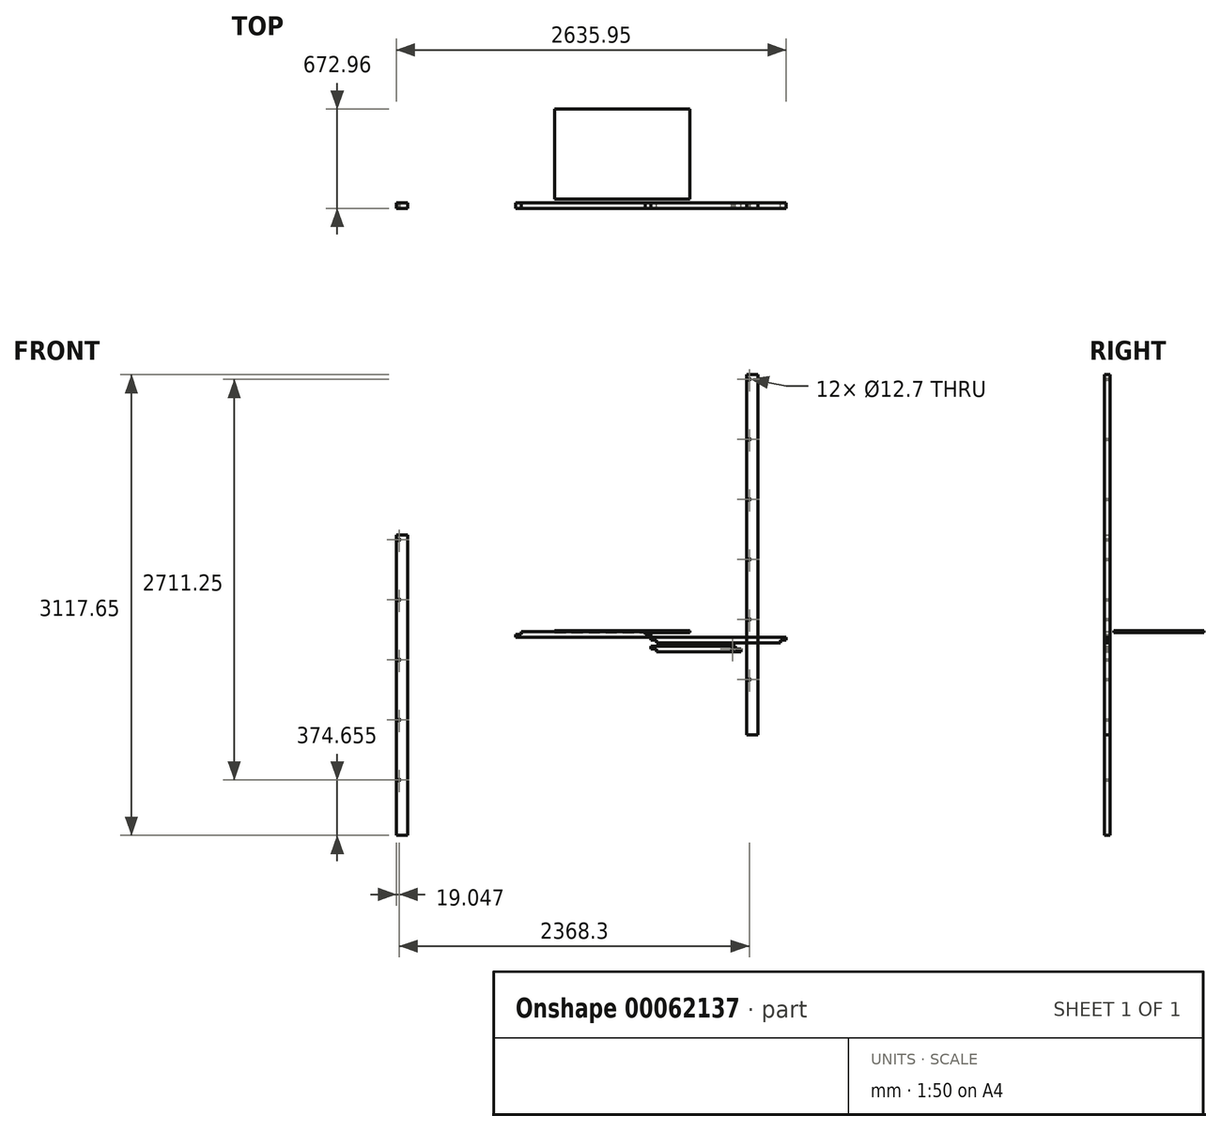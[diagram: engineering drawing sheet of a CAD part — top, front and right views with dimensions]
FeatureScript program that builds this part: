
annotation { "Feature Type Name" : "Feature", "Feature Type Description" : "" }
export const myFeature = defineFeature(function(context is Context, id is Id, definition is map)
    precondition{}
    {
        {
            var Q0;
            Q0=qCreatedBy(makeId("Top.planeOp"),FACE);
            var sketch = newSketch(context, id + "F0", { "sketchPlane" : qUnion([Q0])});
            skLineSegment(sketch, "E0.bottom", {"start": v(-1354.97, 634.86) * mm, "end": v(-440.57, 634.86) * mm});
            skLineSegment(sketch, "E0.top", {"start": v(-1354.97, 25.26) * mm, "end": v(-440.57, 25.26) * mm});
            skLineSegment(sketch, "E0.left", {"start": v(-1354.97, 634.86) * mm, "end": v(-1354.97, 25.26) * mm});
            skLineSegment(sketch, "E0.right", {"start": v(-440.57, 634.86) * mm, "end": v(-440.57, 25.26) * mm});
            skSolve(sketch);
        }
        {
            var Q0;
            Q0=qCreatedBy(makeId("Front.planeOp"),FACE);
            var sketch = newSketch(context, id + "F1", { "sketchPlane" : qUnion([Q0])});
            skLineSegment(sketch, "E1.bottom", {"start": v(-704.43, -92.97) * mm, "end": v(-132.93, -92.97) * mm});
            skLineSegment(sketch, "E1.top", {"start": v(-666.33, -131.07) * mm, "end": v(-94.83, -131.07) * mm});
            skLineSegment(sketch, "E1.left", {"start": v(-704.43, -92.97) * mm, "end": v(-704.43, -112.02) * mm});
            skLineSegment(sketch, "E1.right", {"start": v(-94.83, -112.02) * mm, "end": v(-94.83, -131.07) * mm});
            skLineSegment(sketch, "E2.top", {"start": v(-94.83, -112.02) * mm, "end": v(-132.93, -112.02) * mm});
            skLineSegment(sketch, "E2.right", {"start": v(-132.93, -92.97) * mm, "end": v(-132.93, -112.02) * mm});
            skLineSegment(sketch, "E3.top", {"start": v(-704.43, -112.02) * mm, "end": v(-666.33, -112.02) * mm});
            skLineSegment(sketch, "E3.right", {"start": v(-666.33, -131.07) * mm, "end": v(-666.33, -112.02) * mm});
            skCircle(sketch, "E4", {"center": v(-151.98, -112.02) * mm, "radius": 6.35 * mm});
            skSolve(sketch);
        }
        {
            var Q0;
            Q0=makeQuery(id+"F1.imprint","IMPRINT",FACE,{"disambiguationData":[TD([[makeQuery(id+"F1.imprint","IMPRINT",EDGE,{"derivedFrom":sQuery(id+"F1.wireOp",EDGE,"E1.bottom")}),-1.0]])]});
            extrude(context, id + "F2", {"entities" : qUnion([Q0]), "depth" : 38.1 * mm});
        }
        {
            var Q0;
            Q0=qCreatedBy(makeId("Front.planeOp"),FACE);
            var sketch = newSketch(context, id + "F3", { "sketchPlane" : qUnion([Q0])});
            skLineSegment(sketch, "E5.bottom", {"start": v(-703.85, -31.36) * mm, "end": v(210.55, -31.36) * mm});
            skLineSegment(sketch, "E5.top", {"start": v(-665.75, -69.46) * mm, "end": v(172.45, -69.46) * mm});
            skLineSegment(sketch, "E5.left", {"start": v(-703.85, -31.36) * mm, "end": v(-703.85, -50.4) * mm});
            skLineSegment(sketch, "E5.right", {"start": v(210.55, -31.36) * mm, "end": v(210.55, -50.4) * mm});
            skLineSegment(sketch, "E6.top", {"start": v(210.55, -50.4) * mm, "end": v(172.45, -50.4) * mm});
            skLineSegment(sketch, "E6.right", {"start": v(172.45, -69.46) * mm, "end": v(172.45, -50.4) * mm});
            skLineSegment(sketch, "E7.top", {"start": v(-703.85, -50.4) * mm, "end": v(-665.75, -50.4) * mm});
            skLineSegment(sketch, "E7.right", {"start": v(-665.75, -69.46) * mm, "end": v(-665.75, -50.4) * mm});
            skSolve(sketch);
        }
        {
            var Q0;
            Q0=makeQuery(id+"F3.imprint","IMPRINT",FACE,{"disambiguationData":[TD([[makeQuery(id+"F3.imprint","IMPRINT",EDGE,{"derivedFrom":sQuery(id+"F3.wireOp",EDGE,"E5.bottom")}),-1.0]])]});
            extrude(context, id + "F4", {"entities" : qUnion([Q0]), "depth" : 38.1 * mm});
        }
        {
            var Q0;
            Q0=makeQuery(id+"F4.opExtrude","SWEPT_BODY",BODY,{"disambiguationData":[OSD([sQuery(id+"F3.wireOp",EDGE,"E5.bottom"),sQuery(id+"F3.wireOp",EDGE,"E5.top"),sQuery(id+"F3.wireOp",EDGE,"E5.left"),sQuery(id+"F3.wireOp",EDGE,"E5.right"),sQuery(id+"F3.wireOp",EDGE,"E6.top"),sQuery(id+"F3.wireOp",EDGE,"E6.right"),sQuery(id+"F3.wireOp",EDGE,"E7.top"),sQuery(id+"F3.wireOp",EDGE,"E7.right")])]});
            var Q1;
            Q1=makeQuery(id+"F4.opExtrude","SWEPT_EDGE",EDGE,{"disambiguationData":[OSD([sQuery(id+"F3.wireOp",EDGE,"E5.bottom"),sQuery(id+"F3.wireOp",EDGE,"E5.left")])]});
            transform(context, id + "F5", {"entities" : qUnion([Q0]), "transformType" : TransformType.ROTATION, "transformAxis" : qUnion([Q1]), "angle" : 180 * degree, "makeCopy" : true});
        }
        {
            var Q0;
            Q0 = qSketchRegion(id + "F0", true);
            extrude(context, id + "F6", {"entities" : qUnion([Q0]), "depth" : 12.7 * mm});
        }
        {
            var Q0;
            Q0=qCreatedBy(makeId("Front.planeOp"),FACE);
            var sketch = newSketch(context, id + "F7", { "sketchPlane" : qUnion([Q0])});
            skLineSegment(sketch, "E8.bottom", {"start": v(-57.1, 1745.74) * mm, "end": v(19.1, 1745.74) * mm});
            skLineSegment(sketch, "E8.top", {"start": v(-57.1, -692.66) * mm, "end": v(19.1, -692.66) * mm});
            skLineSegment(sketch, "E8.left", {"start": v(-57.1, 1745.74) * mm, "end": v(-57.1, -692.66) * mm});
            skLineSegment(sketch, "E8.right", {"start": v(19.1, 1745.74) * mm, "end": v(19.1, -692.66) * mm});
            skCircle(sketch, "E9", {"center": v(-38.06, -318) * mm, "radius": 6.35 * mm});
            skPoint(sketch, "E9.centerSnap0", {"position": v(-19, -692.66) * mm});
            skCircle(sketch, "E10.0.1.0", {"center": v(-38.06, 88.4) * mm, "radius": 6.35 * mm});
            skCircle(sketch, "E10.0.2.0", {"center": v(-38.06, 494.8) * mm, "radius": 6.35 * mm});
            skCircle(sketch, "E10.0.3.0", {"center": v(-38.06, 901.2) * mm, "radius": 6.35 * mm});
            skCircle(sketch, "E10.0.4.0", {"center": v(-38.06, 1307.6) * mm, "radius": 6.35 * mm});
            skCircle(sketch, "E10.0.5.0", {"center": v(-38.06, 1714) * mm, "radius": 6.35 * mm});
            skLineSegment(sketch, "E10.direction1", {"start": v(-38.06, -318) * mm, "end": v(-12.66, -318) * mm, "construction": true});
            skLineSegment(sketch, "E10.direction2", {"start": v(-38.06, -318) * mm, "end": v(-38.06, 88.4) * mm, "construction": true});
            skSolve(sketch);
        }
        {
            var Q0;
            Q0=makeQuery(id+"F7.imprint","IMPRINT",FACE,{"disambiguationData":[TD([[makeQuery(id+"F7.imprint","IMPRINT",EDGE,{"derivedFrom":sQuery(id+"F7.wireOp",EDGE,"E8.bottom")}),-1.0]])]});
            extrude(context, id + "F8", {"entities" : qUnion([Q0]), "depth" : 38.1 * mm});
        }
        {
            var Q0;
            Q0=qCreatedBy(makeId("Front.planeOp"),FACE);
            var sketch = newSketch(context, id + "F9", { "sketchPlane" : qUnion([Q0])});
            skLineSegment(sketch, "E11.bottom", {"start": v(-2425.4, 660.1) * mm, "end": v(-2349.2, 660.1) * mm});
            skLineSegment(sketch, "E11.top", {"start": v(-2425.4, -1371.9) * mm, "end": v(-2349.2, -1371.9) * mm});
            skLineSegment(sketch, "E11.left", {"start": v(-2425.4, 660.1) * mm, "end": v(-2425.4, -1371.9) * mm});
            skLineSegment(sketch, "E11.right", {"start": v(-2349.2, 660.1) * mm, "end": v(-2349.2, -1371.9) * mm});
            skCircle(sketch, "E12", {"center": v(-2406.35, -997.26) * mm, "radius": 6.35 * mm});
            skPoint(sketch, "E12.centerSnap0", {"position": v(-2387.3, -1371.9) * mm});
            skCircle(sketch, "E13.0.1.0", {"center": v(-2406.35, -590.86) * mm, "radius": 6.35 * mm});
            skCircle(sketch, "E13.0.2.0", {"center": v(-2406.35, -184.46) * mm, "radius": 6.35 * mm});
            skCircle(sketch, "E13.0.3.0", {"center": v(-2406.35, 221.94) * mm, "radius": 6.35 * mm});
            skCircle(sketch, "E13.0.4.0", {"center": v(-2406.35, 628.34) * mm, "radius": 6.35 * mm});
            skLineSegment(sketch, "E13.direction1", {"start": v(-2406.35, -997.26) * mm, "end": v(-2380.95, -997.26) * mm, "construction": true});
            skLineSegment(sketch, "E13.direction2", {"start": v(-2406.35, -997.26) * mm, "end": v(-2406.35, -590.86) * mm, "construction": true});
            skSolve(sketch);
        }
        {
            var Q0;
            Q0=makeQuery(id+"F9.imprint","IMPRINT",FACE,{"disambiguationData":[TD([[makeQuery(id+"F9.imprint","IMPRINT",EDGE,{"derivedFrom":sQuery(id+"F9.wireOp",EDGE,"E11.bottom")}),-1.0]])]});
            extrude(context, id + "F10", {"entities" : qUnion([Q0]), "depth" : 38.1 * mm});
        }
    });
